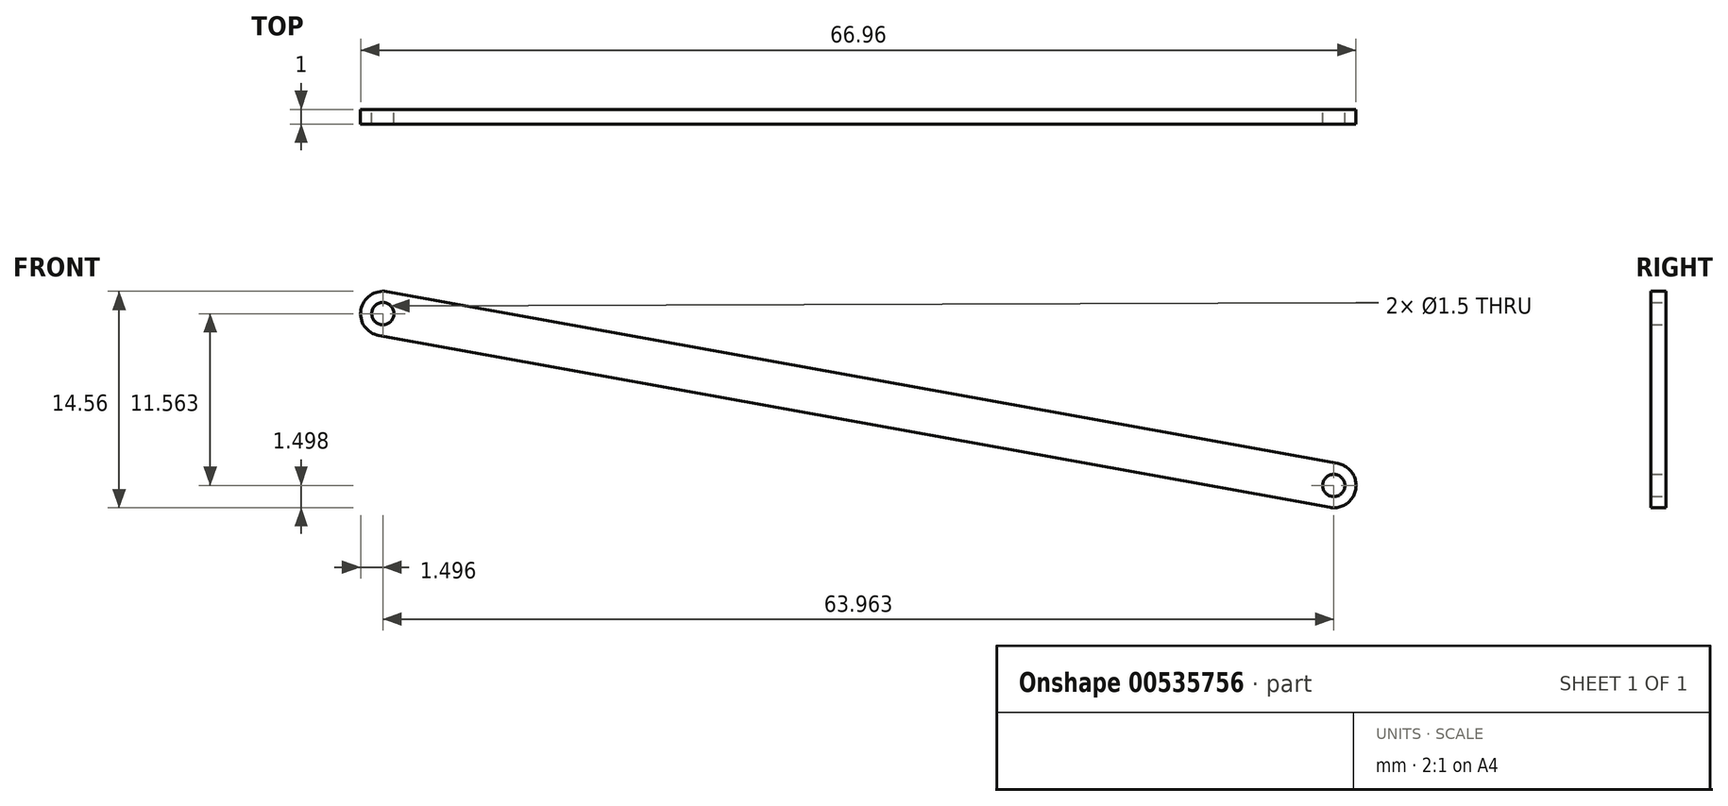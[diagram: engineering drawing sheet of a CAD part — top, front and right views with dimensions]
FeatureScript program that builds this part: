
annotation { "Feature Type Name" : "Feature", "Feature Type Description" : "" }
export const myFeature = defineFeature(function(context is Context, id is Id, definition is map)
    precondition{}
    {
        {
            var Q0;
            Q0=qCreatedBy(makeId("Front.planeOp"),FACE);
            var sketch = newSketch(context, id + "F0", { "sketchPlane" : qUnion([Q0])});
            skCircle(sketch, "E0", {"center": v(-6.7, 14.06) * mm, "radius": 0.75 * mm});
            skArc(sketch, "E1", {"start": v(-6.43, 15.54) * mm, "mid": v(-8.17, 14.33) * mm, "end": v(-6.96, 12.58) * mm});
            skArc(sketch, "E2", {"start": v(57, 1.02) * mm, "mid": v(58.75, 2.23) * mm, "end": v(57.54, 3.97) * mm});
            skCircle(sketch, "E3", {"center": v(57.27, 2.5) * mm, "radius": 0.75 * mm});
            skLineSegment(sketch, "E4", {"start": v(-6.43, 15.54) * mm, "end": v(57.54, 3.97) * mm});
            skLineSegment(sketch, "E5", {"start": v(57, 1.02) * mm, "end": v(-6.96, 12.58) * mm});
            skSolve(sketch);
        }
        {
            var Q0;
            Q0 = qSketchRegion(id + "F0", true);
            extrude(context, id + "F1", {"entities" : qUnion([Q0]), "endBound" : BoundingType.SYMMETRIC, "depth" : 1 * mm, "offsetDistance" : 25 * mm});
        }
    });
